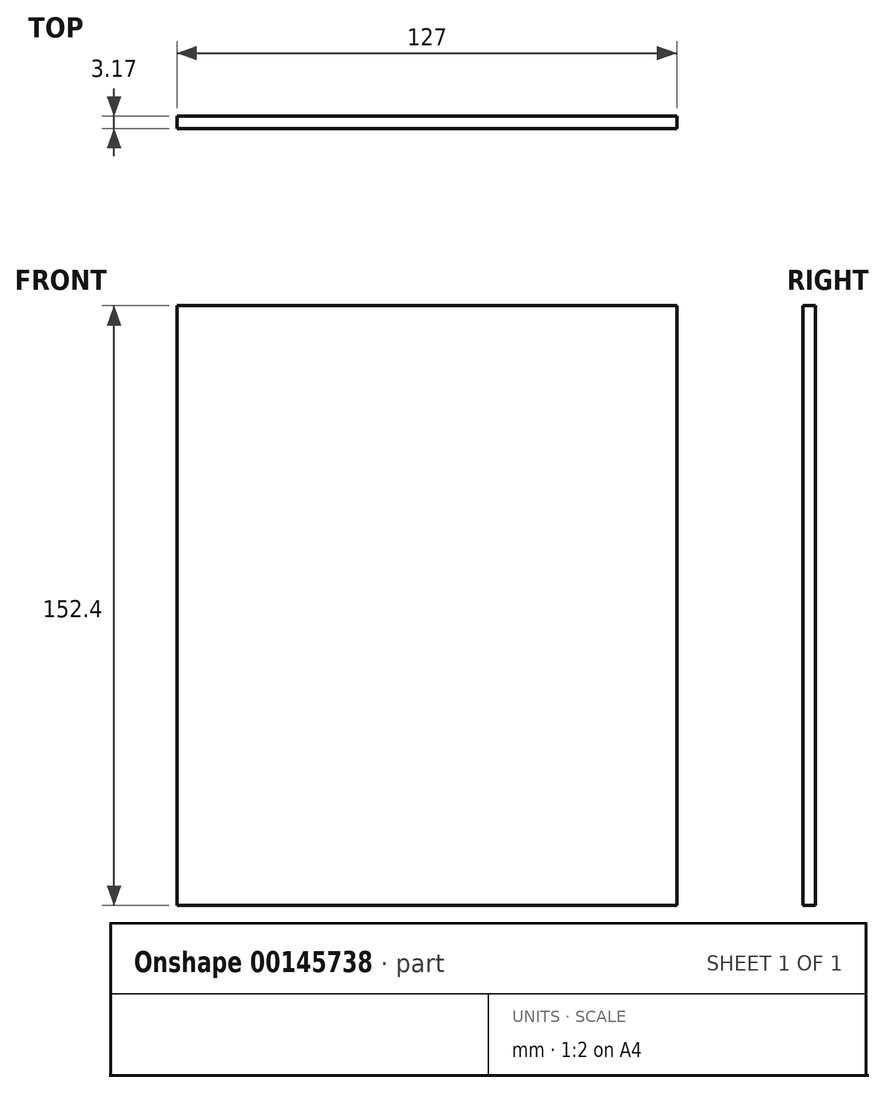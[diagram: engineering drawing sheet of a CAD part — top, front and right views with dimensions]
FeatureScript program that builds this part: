
annotation { "Feature Type Name" : "Feature", "Feature Type Description" : "" }
export const myFeature = defineFeature(function(context is Context, id is Id, definition is map)
    precondition{}
    {
        {
            var Q0;
            Q0=qCreatedBy(makeId("Front.planeOp"),FACE);
            var sketch = newSketch(context, id + "F0", { "sketchPlane" : qUnion([Q0])});
            skLineSegment(sketch, "E0.bottom", {"start": v(0, 0) * mm, "end": v(-127, 0) * mm});
            skLineSegment(sketch, "E0.top", {"start": v(0, 152.4) * mm, "end": v(-127, 152.4) * mm});
            skLineSegment(sketch, "E0.left", {"start": v(0, 0) * mm, "end": v(0, 152.4) * mm});
            skLineSegment(sketch, "E0.right", {"start": v(-127, 0) * mm, "end": v(-127, 152.4) * mm});
            skSolve(sketch);
        }
        {
            var Q0;
            Q0=makeQuery(id+"F0.imprint","IMPRINT",FACE,{"disambiguationData":[TD([[makeQuery(id+"F0.imprint","IMPRINT",EDGE,{"derivedFrom":sQuery(id+"F0.wireOp",EDGE,"E0.bottom")}),-1.0]])]});
            extrude(context, id + "F1", {"entities" : qUnion([Q0]), "depth" : 3.17 * mm});
        }
    });
